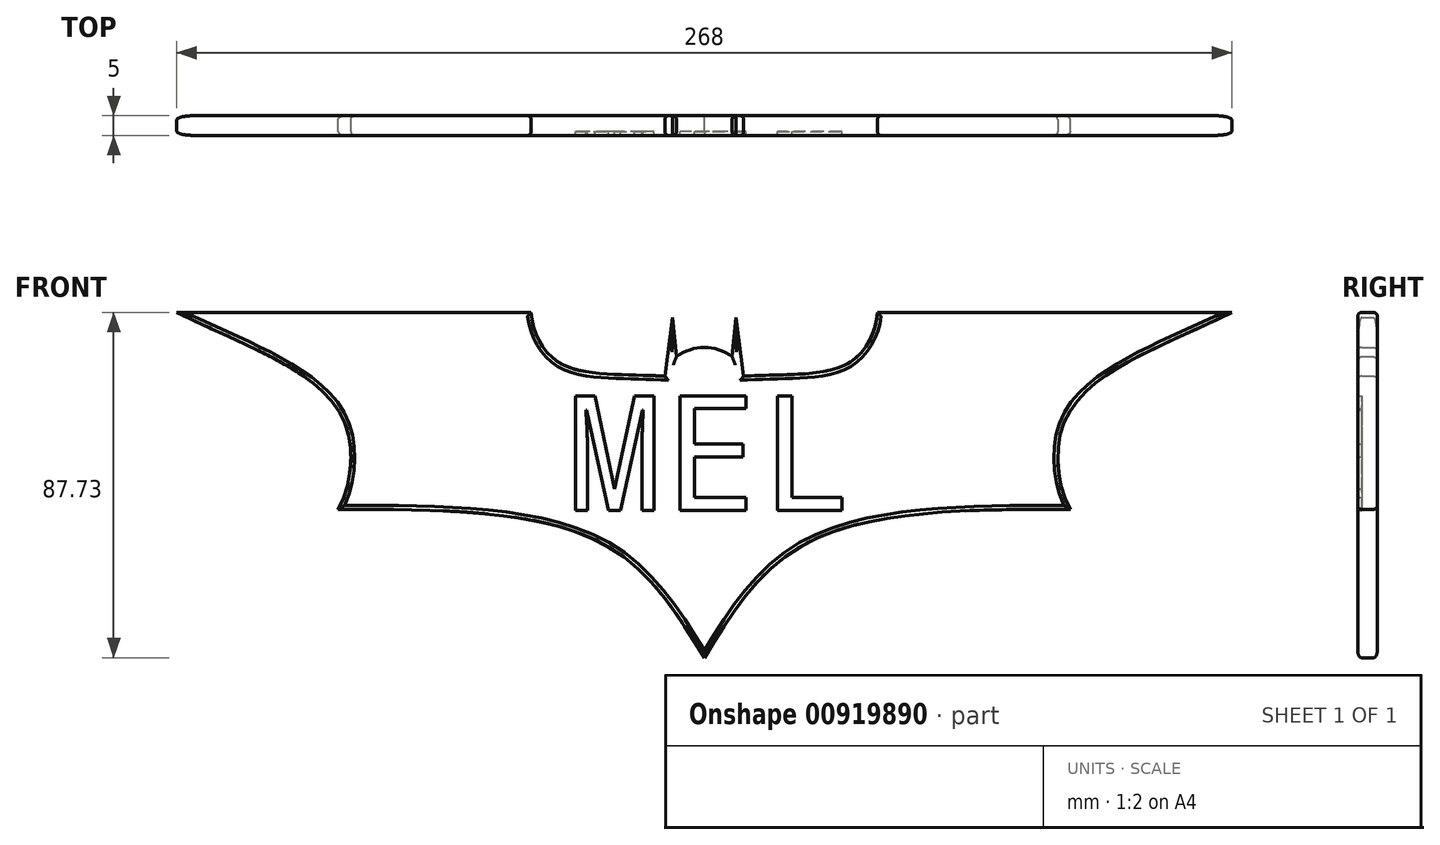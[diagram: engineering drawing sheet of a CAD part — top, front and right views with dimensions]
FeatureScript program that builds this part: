
annotation { "Feature Type Name" : "Feature", "Feature Type Description" : "" }
export const myFeature = defineFeature(function(context is Context, id is Id, definition is map)
    precondition{}
    {
        {
            var Q0;
            Q0=qCreatedBy(makeId("Front.planeOp"),FACE);
            var sketch = newSketch(context, id + "F0", { "sketchPlane" : qUnion([Q0])});
            skArc(sketch, "E0", {"start": v(7.06, 43.8) * mm, "mid": v(0, 46.17) * mm, "end": v(-7.06, 43.8) * mm});
            skLineSegment(sketch, "E1", {"start": v(-7.06, 43.8) * mm, "end": v(-8.09, 53.75) * mm});
            skLineSegment(sketch, "E2", {"start": v(-8.09, 53.75) * mm, "end": v(-10, 38.88) * mm});
            skFitSpline(sketch, "E3", {"points": [v(-10, 38.88) * mm, v(-36.7, 42.22) * mm, v(-44, 55.04) * mm], "startDerivative": vector(-67.87, 3.06) * mm, "endDerivative": vector(-3.47, 40.54) * mm});
            skLineSegment(sketch, "E4", {"start": v(-44, 55.04) * mm, "end": v(-134, 55.04) * mm});
            skFitSpline(sketch, "E5", {"points": [v(-134, 55.04) * mm, v(-92.16, 28.77) * mm, v(-93, 5.04) * mm], "startDerivative": vector(83.7, -40.96) * mm, "endDerivative": vector(-21.5, -36.05) * mm});
            skFitSpline(sketch, "E6", {"points": [v(-93, 5.04) * mm, v(-26.28, -3.43) * mm, v(0, -32.69) * mm], "startDerivative": vector(133.91, -0.06) * mm, "endDerivative": vector(48.28, -78.9) * mm});
            skFitSpline(sketch, "E7.MirrorCS", {"points": [v(93, 5.04) * mm, v(26.28, -3.43) * mm, v(0, -32.69) * mm], "startDerivative": vector(-133.91, -0.06) * mm, "endDerivative": vector(-48.28, -78.9) * mm});
            skFitSpline(sketch, "E8.MirrorCS", {"points": [v(134, 55.04) * mm, v(92.16, 28.77) * mm, v(93, 5.04) * mm], "startDerivative": vector(-83.7, -40.96) * mm, "endDerivative": vector(21.5, -36.05) * mm});
            skLineSegment(sketch, "E9.MirrorCS", {"start": v(44, 55.04) * mm, "end": v(134, 55.04) * mm});
            skFitSpline(sketch, "E10.MirrorCS", {"points": [v(10, 38.88) * mm, v(36.7, 42.22) * mm, v(44, 55.04) * mm], "startDerivative": vector(67.87, 3.06) * mm, "endDerivative": vector(3.47, 40.54) * mm});
            skLineSegment(sketch, "E11.MirrorCS", {"start": v(7.06, 43.8) * mm, "end": v(8.09, 53.75) * mm});
            skLineSegment(sketch, "E12.MirrorCS", {"start": v(8.09, 53.75) * mm, "end": v(10, 38.88) * mm});
            skSolve(sketch);
        }
        {
            var Q0;
            Q0=makeQuery(id+"F0.imprint","IMPRINT",FACE,{"disambiguationData":[TD([[makeQuery(id+"F0.imprint","IMPRINT",EDGE,{"derivedFrom":sQuery(id+"F0.wireOp",EDGE,"E0")}),1.0]])]});
            extrude(context, id + "F1", {"entities" : qUnion([Q0]), "depth" : 5 * mm});
        }
        {
            var Q0;
            Q0=qCreatedBy(makeId("Front.planeOp"),FACE);
            var sketch = newSketch(context, id + "F2", { "sketchPlane" : qUnion([Q0])});
            skText(sketch, "E13", { "text": "MEL", "fontName": "DroidSansMono.ttf"});
            const initialGuessF2  = {"E13": [-0.03497, 0.00478, 1, 0, 0.02935]};
            skSetInitialGuess(sketch, initialGuessF2);
            skSolve(sketch);
        }
        {
            var Q0;
            Q0=qSketchRegion(id+"F2",true);
            extrude(context, id + "F3", {"entities" : qUnion([Q0]), "operationType" : NewBodyOperationType.REMOVE, "depth" : 5 * mm, "hasSecondDirection" : true, "secondDirectionOppositeDirection" : false, "secondDirectionDepth" : 4 * mm});
        }
        {
            var Q0;
            Q0=makeQuery(id+"F1.opExtrude","CAP_EDGE",EDGE,{"disambiguationData":[OSD([sQuery(id+"F0.wireOp",EDGE,"E4")])],"isStart":false});
            var Q1;
            Q1=makeQuery(id+"F1.opExtrude","CAP_EDGE",EDGE,{"disambiguationData":[OSD([sQuery(id+"F0.wireOp",EDGE,"E5")])],"isStart":false});
            var Q2;
            Q2=makeQuery(id+"F1.opExtrude","CAP_EDGE",EDGE,{"disambiguationData":[OSD([sQuery(id+"F0.wireOp",EDGE,"E6")])],"isStart":false});
            var Q3;
            Q3=makeQuery(id+"F1.opExtrude","CAP_EDGE",EDGE,{"disambiguationData":[OSD([sQuery(id+"F0.wireOp",EDGE,"E7.MirrorCS")])],"isStart":false});
            var Q4;
            Q4=makeQuery(id+"F1.opExtrude","CAP_EDGE",EDGE,{"disambiguationData":[OSD([sQuery(id+"F0.wireOp",EDGE,"E8.MirrorCS")])],"isStart":false});
            var Q5;
            Q5=makeQuery(id+"F1.opExtrude","CAP_EDGE",EDGE,{"disambiguationData":[OSD([sQuery(id+"F0.wireOp",EDGE,"E9.MirrorCS")])],"isStart":false});
            var Q6;
            Q6=makeQuery(id+"F1.opExtrude","CAP_EDGE",EDGE,{"disambiguationData":[OSD([sQuery(id+"F0.wireOp",EDGE,"E11.MirrorCS")])],"isStart":false});
            var Q7;
            Q7=makeQuery(id+"F1.opExtrude","CAP_EDGE",EDGE,{"disambiguationData":[OSD([sQuery(id+"F0.wireOp",EDGE,"E1")])],"isStart":false});
            var Q8;
            Q8=makeQuery(id+"F1.opExtrude","CAP_EDGE",EDGE,{"disambiguationData":[OSD([sQuery(id+"F0.wireOp",EDGE,"E0")])],"isStart":false});
            var Q9;
            Q9=makeQuery(id+"F1.opExtrude","CAP_EDGE",EDGE,{"disambiguationData":[OSD([sQuery(id+"F0.wireOp",EDGE,"E2")])],"isStart":false});
            var Q10;
            Q10=makeQuery(id+"F1.opExtrude","CAP_EDGE",EDGE,{"disambiguationData":[OSD([sQuery(id+"F0.wireOp",EDGE,"E12.MirrorCS")])],"isStart":false});
            var Q11;
            Q11=makeQuery(id+"F1.opExtrude","CAP_EDGE",EDGE,{"disambiguationData":[OSD([sQuery(id+"F0.wireOp",EDGE,"E10.MirrorCS")])],"isStart":false});
            var Q12;
            Q12=makeQuery(id+"F1.opExtrude","CAP_EDGE",EDGE,{"disambiguationData":[OSD([sQuery(id+"F0.wireOp",EDGE,"E3")])],"isStart":false});
            var Q13;
            Q13=makeQuery(id+"F1.opExtrude","CAP_EDGE",EDGE,{"disambiguationData":[OSD([sQuery(id+"F0.wireOp",EDGE,"E12.MirrorCS")])],"isStart":true});
            var Q14;
            Q14=makeQuery(id+"F1.opExtrude","CAP_EDGE",EDGE,{"disambiguationData":[OSD([sQuery(id+"F0.wireOp",EDGE,"E11.MirrorCS")])],"isStart":true});
            var Q15;
            Q15=makeQuery(id+"F1.opExtrude","CAP_EDGE",EDGE,{"disambiguationData":[OSD([sQuery(id+"F0.wireOp",EDGE,"E0")])],"isStart":true});
            var Q16;
            Q16=makeQuery(id+"F1.opExtrude","CAP_EDGE",EDGE,{"disambiguationData":[OSD([sQuery(id+"F0.wireOp",EDGE,"E1")])],"isStart":true});
            var Q17;
            Q17=makeQuery(id+"F1.opExtrude","CAP_EDGE",EDGE,{"disambiguationData":[OSD([sQuery(id+"F0.wireOp",EDGE,"E2")])],"isStart":true});
            var Q18;
            Q18=makeQuery(id+"F1.opExtrude","CAP_EDGE",EDGE,{"disambiguationData":[OSD([sQuery(id+"F0.wireOp",EDGE,"E3")])],"isStart":true});
            var Q19;
            Q19=makeQuery(id+"F1.opExtrude","CAP_EDGE",EDGE,{"disambiguationData":[OSD([sQuery(id+"F0.wireOp",EDGE,"E10.MirrorCS")])],"isStart":true});
            var Q20;
            Q20=makeQuery(id+"F1.opExtrude","CAP_EDGE",EDGE,{"disambiguationData":[OSD([sQuery(id+"F0.wireOp",EDGE,"E9.MirrorCS")])],"isStart":true});
            var Q21;
            Q21=makeQuery(id+"F1.opExtrude","CAP_EDGE",EDGE,{"disambiguationData":[OSD([sQuery(id+"F0.wireOp",EDGE,"E8.MirrorCS")])],"isStart":true});
            var Q22;
            Q22=makeQuery(id+"F1.opExtrude","CAP_EDGE",EDGE,{"disambiguationData":[OSD([sQuery(id+"F0.wireOp",EDGE,"E7.MirrorCS")])],"isStart":true});
            var Q23;
            Q23=makeQuery(id+"F1.opExtrude","CAP_EDGE",EDGE,{"disambiguationData":[OSD([sQuery(id+"F0.wireOp",EDGE,"E6")])],"isStart":true});
            var Q24;
            Q24=makeQuery(id+"F1.opExtrude","CAP_EDGE",EDGE,{"disambiguationData":[OSD([sQuery(id+"F0.wireOp",EDGE,"E5")])],"isStart":true});
            var Q25;
            Q25=makeQuery(id+"F1.opExtrude","CAP_EDGE",EDGE,{"disambiguationData":[OSD([sQuery(id+"F0.wireOp",EDGE,"E4")])],"isStart":true});
            fillet(context, id + "F4", {"entities" : qUnion([Q0, Q1, Q2, Q3, Q4, Q5, Q6, Q7, Q8, Q9, Q10, Q11, Q12, Q13, Q14, Q15, Q16, Q17, Q18, Q19, Q20, Q21, Q22, Q23, Q24, Q25]), "radius" : 1 * mm, "tangentPropagation" : true, "allowEdgeOverflow" : false});
        }
    });
